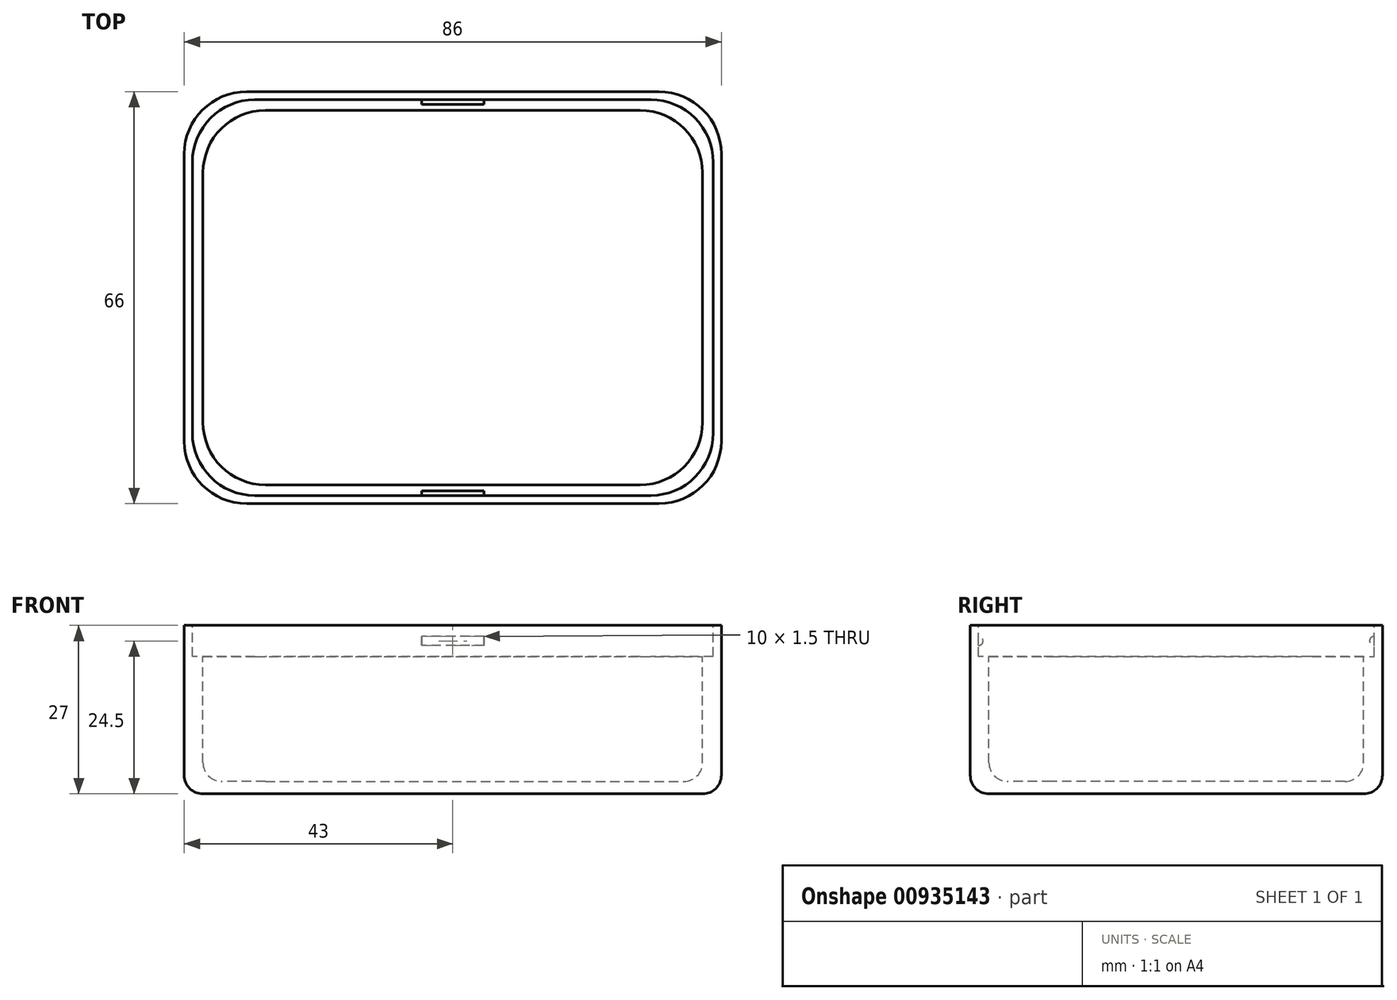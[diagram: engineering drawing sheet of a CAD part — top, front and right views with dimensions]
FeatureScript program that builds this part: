
annotation { "Feature Type Name" : "Feature", "Feature Type Description" : "" }
export const myFeature = defineFeature(function(context is Context, id is Id, definition is map)
    precondition{}
    {
        {
            var Q0;
            Q0=qCreatedBy(makeId("Top.planeOp"),FACE);
            var sketch = newSketch(context, id + "F0", { "sketchPlane" : qUnion([Q0])});
            skLineSegment(sketch, "E0.bottom", {"start": v(10, 0) * mm, "end": v(76, 0) * mm});
            skLineSegment(sketch, "E0.top", {"start": v(10, -66) * mm, "end": v(76, -66) * mm});
            skLineSegment(sketch, "E0.left", {"start": v(0, -10) * mm, "end": v(0, -56) * mm});
            skLineSegment(sketch, "E0.right", {"start": v(86, -10) * mm, "end": v(86, -56) * mm});
            skPoint(sketch, "E1.visualSharp", {"position": v(0, 0) * mm});
            skArc(sketch, "E1.filletArc", {"start": v(10, 0) * mm, "mid": v(2.93, -2.93) * mm, "end": v(0, -10) * mm});
            skPoint(sketch, "E2.visualSharp", {"position": v(86, 0) * mm});
            skArc(sketch, "E2.filletArc", {"start": v(86, -10) * mm, "mid": v(83.07, -2.93) * mm, "end": v(76, 0) * mm});
            skPoint(sketch, "E3.visualSharp", {"position": v(86, -66) * mm});
            skArc(sketch, "E3.filletArc", {"start": v(76, -66) * mm, "mid": v(83.07, -63.07) * mm, "end": v(86, -56) * mm});
            skPoint(sketch, "E4.visualSharp", {"position": v(0, -66) * mm});
            skArc(sketch, "E4.filletArc", {"start": v(0, -56) * mm, "mid": v(2.93, -63.07) * mm, "end": v(10, -66) * mm});
            skSolve(sketch);
        }
        {
            var Q0;
            Q0=qSketchRegion(id+"F0",true);
            extrude(context, id + "F1", {"entities" : qUnion([Q0]), "depth" : 27 * mm, "offsetDistance" : 25.4 * mm});
        }
        {
            var Q0;
            Q0=makeQuery(id+"F1.opExtrude","CAP_FACE",FACE,{"disambiguationData":[OSD([sQuery(id+"F0.wireOp",EDGE,"E0.bottom"),sQuery(id+"F0.wireOp",EDGE,"E0.top"),sQuery(id+"F0.wireOp",EDGE,"E0.left"),sQuery(id+"F0.wireOp",EDGE,"E0.right")])],"isStart":false});
            var sketch = newSketch(context, id + "F2", { "sketchPlane" : qUnion([Q0])});
            skLineSegment(sketch, "E5.bottom", {"start": v(13, -3) * mm, "end": v(73, -3) * mm});
            skLineSegment(sketch, "E5.top", {"start": v(13, -63) * mm, "end": v(73, -63) * mm});
            skLineSegment(sketch, "E5.left", {"start": v(3, -13) * mm, "end": v(3, -53) * mm});
            skLineSegment(sketch, "E5.right", {"start": v(83, -13) * mm, "end": v(83, -53) * mm});
            skPoint(sketch, "E6.visualSharp", {"position": v(3, -3) * mm});
            skArc(sketch, "E6.filletArc", {"start": v(13, -3) * mm, "mid": v(5.93, -5.93) * mm, "end": v(3, -13) * mm});
            skPoint(sketch, "E7.visualSharp", {"position": v(83, -3) * mm});
            skArc(sketch, "E7.filletArc", {"start": v(83, -13) * mm, "mid": v(80.07, -5.93) * mm, "end": v(73, -3) * mm});
            skPoint(sketch, "E8.visualSharp", {"position": v(83, -63) * mm});
            skArc(sketch, "E8.filletArc", {"start": v(73, -63) * mm, "mid": v(80.07, -60.07) * mm, "end": v(83, -53) * mm});
            skPoint(sketch, "E9.visualSharp", {"position": v(3, -63) * mm});
            skArc(sketch, "E9.filletArc", {"start": v(3, -53) * mm, "mid": v(5.93, -60.07) * mm, "end": v(13, -63) * mm});
            skSolve(sketch);
        }
        {
            var Q0;
            Q0=qSketchRegion(id+"F2",true);
            extrude(context, id + "F3", {"entities" : qUnion([Q0]), "operationType" : NewBodyOperationType.REMOVE, "oppositeDirection" : true, "depth" : 25 * mm, "offsetDistance" : 25.4 * mm});
        }
        {
            var Q0;
            Q0=makeQuery(id+"F1.opExtrude","CAP_FACE",FACE,{"disambiguationData":[OSD([sQuery(id+"F0.wireOp",EDGE,"E0.bottom"),sQuery(id+"F0.wireOp",EDGE,"E0.top"),sQuery(id+"F0.wireOp",EDGE,"E0.left"),sQuery(id+"F0.wireOp",EDGE,"E0.right")])],"isStart":false});
            var sketch = newSketch(context, id + "F4", { "sketchPlane" : qUnion([Q0])});
            skLineSegment(sketch, "E10.bottom", {"start": v(11.3, -1.3) * mm, "end": v(74.7, -1.3) * mm});
            skLineSegment(sketch, "E10.top", {"start": v(11.3, -64.7) * mm, "end": v(74.7, -64.7) * mm});
            skLineSegment(sketch, "E10.left", {"start": v(1.3, -11.3) * mm, "end": v(1.3, -54.7) * mm});
            skLineSegment(sketch, "E10.right", {"start": v(84.7, -11.3) * mm, "end": v(84.7, -54.7) * mm});
            skPoint(sketch, "E11.visualSharp", {"position": v(1.3, -1.3) * mm});
            skArc(sketch, "E11.filletArc", {"start": v(11.3, -1.3) * mm, "mid": v(4.23, -4.23) * mm, "end": v(1.3, -11.3) * mm});
            skPoint(sketch, "E12.visualSharp", {"position": v(84.7, -1.3) * mm});
            skArc(sketch, "E12.filletArc", {"start": v(84.7, -11.3) * mm, "mid": v(81.77, -4.23) * mm, "end": v(74.7, -1.3) * mm});
            skPoint(sketch, "E13.visualSharp", {"position": v(84.7, -64.7) * mm});
            skArc(sketch, "E13.filletArc", {"start": v(74.7, -64.7) * mm, "mid": v(81.77, -61.77) * mm, "end": v(84.7, -54.7) * mm});
            skPoint(sketch, "E14.visualSharp", {"position": v(1.3, -64.7) * mm});
            skArc(sketch, "E14.filletArc", {"start": v(1.3, -54.7) * mm, "mid": v(4.23, -61.77) * mm, "end": v(11.3, -64.7) * mm});
            skSolve(sketch);
        }
        {
            var Q0;
            Q0=qSketchRegion(id+"F4",true);
            extrude(context, id + "F5", {"entities" : qUnion([Q0]), "operationType" : NewBodyOperationType.REMOVE, "oppositeDirection" : true, "depth" : 5 * mm, "offsetDistance" : 25.4 * mm});
        }
        {
            var Q0;
            Q0=makeQuery(id+"F1.opExtrude","CAP_EDGE",EDGE,{"disambiguationData":[OSD([sQuery(id+"F0.wireOp",EDGE,"E0.bottom")])],"isStart":true});
            var Q1;
            Q1=makeQuery(id+"F1.opExtrude","CAP_EDGE",EDGE,{"disambiguationData":[OSD([sQuery(id+"F0.wireOp",EDGE,"E1.filletArc")])],"isStart":true});
            var Q2;
            Q2=makeQuery(id+"F1.opExtrude","CAP_EDGE",EDGE,{"disambiguationData":[OSD([sQuery(id+"F0.wireOp",EDGE,"E0.left")])],"isStart":true});
            var Q3;
            Q3=makeQuery(id+"F1.opExtrude","CAP_EDGE",EDGE,{"disambiguationData":[OSD([sQuery(id+"F0.wireOp",EDGE,"E2.filletArc")])],"isStart":true});
            var Q4;
            Q4=makeQuery(id+"F1.opExtrude","CAP_EDGE",EDGE,{"disambiguationData":[OSD([sQuery(id+"F0.wireOp",EDGE,"E0.right")])],"isStart":true});
            var Q5;
            Q5=makeQuery(id+"F1.opExtrude","CAP_EDGE",EDGE,{"disambiguationData":[OSD([sQuery(id+"F0.wireOp",EDGE,"E3.filletArc")])],"isStart":true});
            var Q6;
            Q6=makeQuery(id+"F1.opExtrude","CAP_EDGE",EDGE,{"disambiguationData":[OSD([sQuery(id+"F0.wireOp",EDGE,"E0.top")])],"isStart":true});
            var Q7;
            Q7=makeQuery(id+"F1.opExtrude","CAP_EDGE",EDGE,{"disambiguationData":[OSD([sQuery(id+"F0.wireOp",EDGE,"E4.filletArc")])],"isStart":true});
            fillet(context, id + "F6", {"entities" : qUnion([Q0, Q1, Q2, Q3, Q4, Q5, Q6, Q7]), "radius" : 3 * mm, "tangentPropagation" : true, "allowEdgeOverflow" : false});
        }
        {
            var Q0;
            Q0=makeQuery(id+"F3.boolean.opBoolean","COPY",EDGE,{"derivedFrom":makeQuery(id+"F3.opExtrude","CAP_EDGE",EDGE,{"disambiguationData":[OSD([sQuery(id+"F2.wireOp",EDGE,"E5.bottom")])],"isStart":false})});
            fillet(context, id + "F7", {"entities" : qUnion([Q0]), "radius" : 3 * mm, "tangentPropagation" : true, "allowEdgeOverflow" : false});
        }
        {
            var Q0;
            Q0=qCreatedBy(makeId("Right.planeOp"),FACE);
            cPlane(context, id + "F8", {"entities" : qUnion([Q0]), "cplaneType" : CPlaneType.OFFSET, "offset" : 43 * mm, "width" : 150 * mm, "height" : 150 * mm});
        }
        {
            var Q0;
            Q0=qCreatedBy(id+"F8.planeOp",FACE);
            var sketch = newSketch(context, id + "F9", { "sketchPlane" : qUnion([Q0])});
            skCircle(sketch, "E15", {"center": v(-1.3, 24.5) * mm, "radius": 0.75 * mm});
            skLineSegment(sketch, "E16", {"start": v(-33, 36.8) * mm, "end": v(-33, -4.96) * mm, "construction": true});
            skCircle(sketch, "E17.MirrorC", {"center": v(-64.7, 24.5) * mm, "radius": 0.75 * mm});
            skSolve(sketch);
        }
        {
            var Q0;
            Q0 = qSketchRegion(id + "F9", true);
            extrude(context, id + "F10", {"entities" : qUnion([Q0]), "operationType" : NewBodyOperationType.ADD, "endBound" : BoundingType.SYMMETRIC, "depth" : 10 * mm, "offsetDistance" : 25 * mm});
        }
    });
